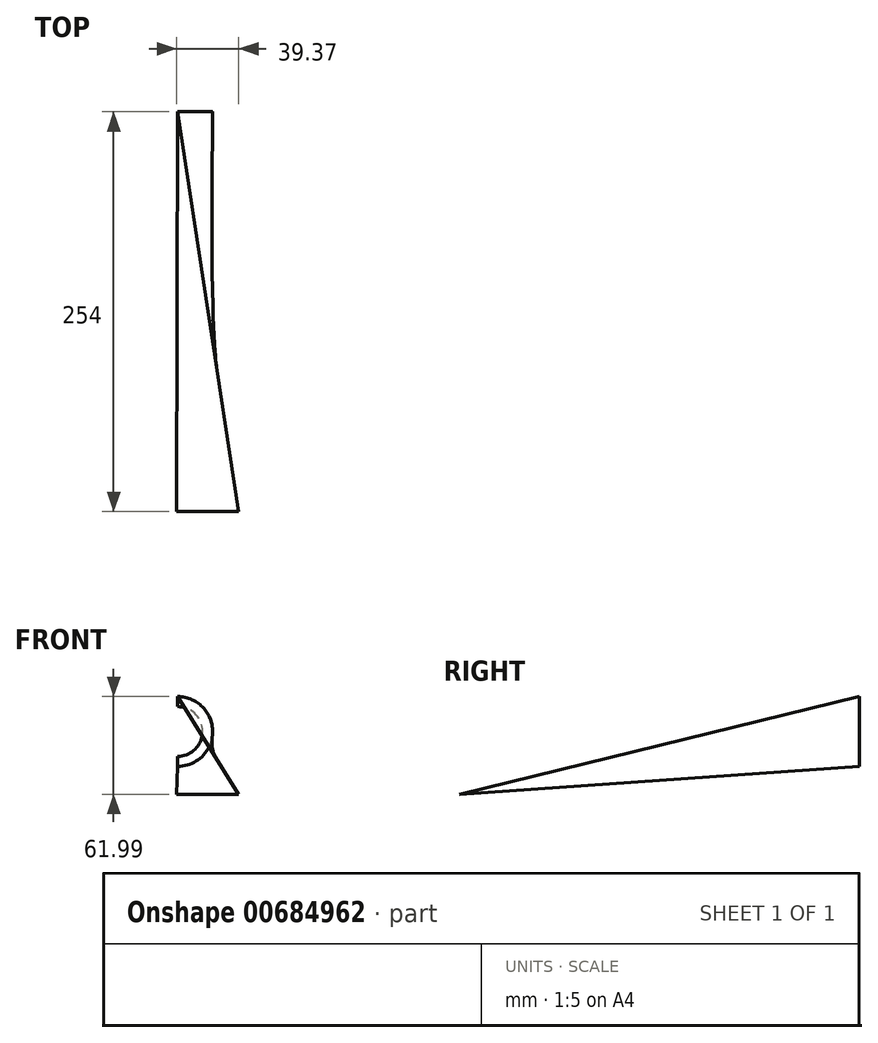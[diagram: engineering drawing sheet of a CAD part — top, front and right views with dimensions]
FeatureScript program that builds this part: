
annotation { "Feature Type Name" : "Feature", "Feature Type Description" : "" }
export const myFeature = defineFeature(function(context is Context, id is Id, definition is map)
    precondition{}
    {
        {
            var Q0;
            Q0=qCreatedBy(makeId("Front.planeOp"),FACE);
            cPlane(context, id + "F0", {"entities" : qUnion([Q0]), "cplaneType" : CPlaneType.OFFSET, "offset" : 254 * mm, "width" : 152.4 * mm, "height" : 152.4 * mm});
        }
        {
            var Q0;
            Q0=qCreatedBy(id+"F0.planeOp",FACE);
            var sketch = newSketch(context, id + "F1", { "sketchPlane" : qUnion([Q0])});
            skLineSegment(sketch, "E0.bottom", {"start": v(-0.66, -33.47) * mm, "end": v(-40.03, -33.47) * mm});
            skLineSegment(sketch, "E0.top", {"start": v(-0.66, -39.82) * mm, "end": v(-40.03, -39.82) * mm});
            skLineSegment(sketch, "E0.left", {"start": v(-0.66, -33.47) * mm, "end": v(-0.66, -39.82) * mm});
            skLineSegment(sketch, "E0.right", {"start": v(-40.03, -33.47) * mm, "end": v(-40.03, -39.82) * mm});
            skLineSegment(sketch, "E1.bottom", {"start": v(-0.66, -33.47) * mm, "end": v(38.71, -33.47) * mm});
            skLineSegment(sketch, "E1.top", {"start": v(-0.66, -39.82) * mm, "end": v(38.71, -39.82) * mm});
            skLineSegment(sketch, "E1.right", {"start": v(38.71, -33.47) * mm, "end": v(38.71, -39.82) * mm});
            skSolve(sketch);
        }
        {
            var Q0;
            Q0=qCreatedBy(makeId("Front.planeOp"),FACE);
            var sketch = newSketch(context, id + "F2", { "sketchPlane" : qUnion([Q0])});
            skLineSegment(sketch, "E2", {"start": v(22.17, 0) * mm, "end": v(15.82, 0) * mm});
            skSolve(sketch);
        }
        {
            var Q0;
            Q0=qCreatedBy(makeId("Top.planeOp"),FACE);
            var sketch = newSketch(context, id + "F3", { "sketchPlane" : qUnion([Q0])});
            skLineSegment(sketch, "E3", {"start": v(0, 8.88) * mm, "end": v(0, -9.85) * mm});
            skSolve(sketch);
        }
        {
            var Q0;
            Q0=qSketchRegion(id+"F2",true);
            var Q1;
            Q1=sQuery(id+"F2.wireOp",EDGE,"E2");
            var Q2;
            Q2=sQuery(id+"F3.wireOp",EDGE,"E3");
            revolve(context, id + "F4", {"bodyType" : ToolBodyType.SURFACE, "entities" : qUnion([Q0]), "surfaceEntities" : qUnion([Q1]), "axis" : qUnion([Q2]), "revolveType" : RevolveType.SYMMETRIC, "angle" : 180 * degree});
        }
        {
            var Q0;
            Q0=makeQuery(id+"F1.imprint","IMPRINT",FACE,{"disambiguationData":[TD([[makeQuery(id+"F1.imprint","IMPRINT",EDGE,{"derivedFrom":sQuery(id+"F1.wireOp",EDGE,"E1.bottom")}),-1.0]])]});
            var Q1;
            Q1=makeQuery(id+"F4.opRevolve","SWEPT_BODY",BODY,{"disambiguationData":[OSD([sQuery(id+"F2.wireOp",EDGE,"E2")])]});
            var Q2;
            Q2=sQuery(id+"F1.wireOp",EDGE,"E1.top");
            var Q3;
            Q3=makeQuery(id+"F4.opRevolve","SWEPT_EDGE",EDGE,{"disambiguationData":[OSD([sQuery(id+"F2.wireOp",VERTEX,"E2.start")])]});
            loft(context, id + "F5", {"bodyType" : ToolBodyType.SURFACE, "sheetProfilesArray" : [{ "sheetProfileEntities" : qUnion([Q0]) }, { "sheetProfileEntities" : qUnion([Q1]) }], "wireProfilesArray" : [{ "wireProfileEntities" : qUnion([Q2]) }, { "wireProfileEntities" : qUnion([Q3]) }]});
        }
    });
